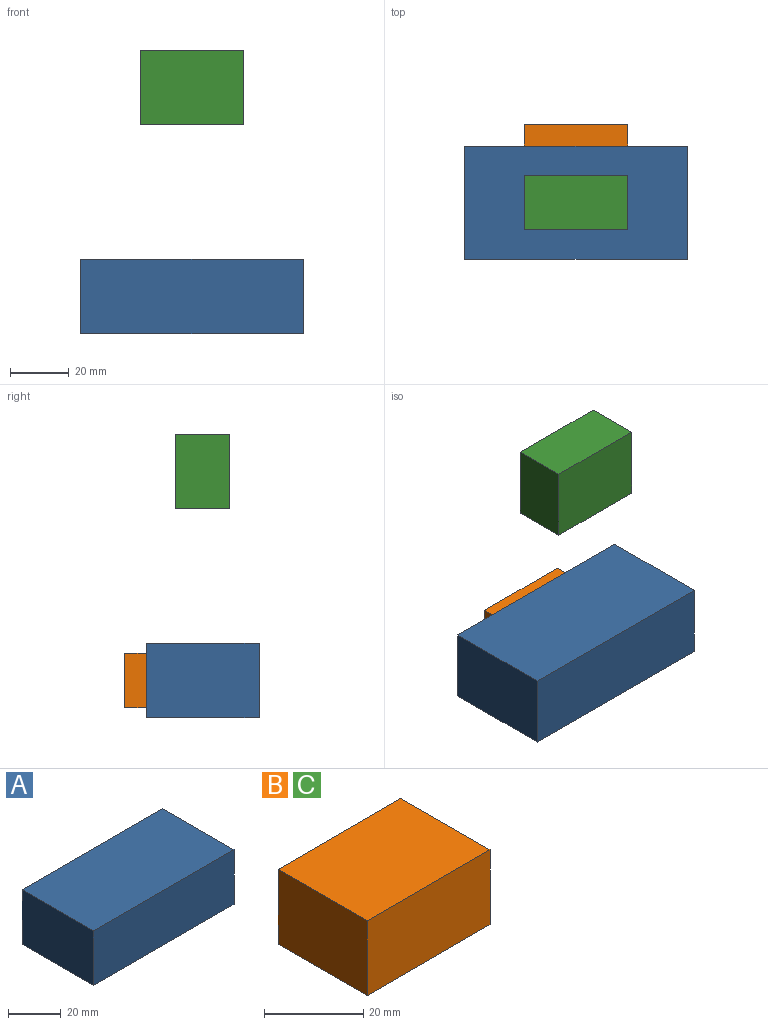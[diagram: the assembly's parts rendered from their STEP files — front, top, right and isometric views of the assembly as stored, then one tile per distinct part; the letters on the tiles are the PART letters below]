
ASSEMBLY  parts=3 mates=2
PART A: 6 faces, bbox 75.6x38.4x25.4 mm
  f0: plane 75.64x25.4mm, normal (0,1,0), area 1921.3mm2, adj f1,f3,f4,f5
  f1: plane 38.41x25.4mm, normal (-1,0,0), area 975.7mm2, adj f0,f2,f4,f5
  f2: plane 75.64x25.4mm, normal (0,-1,0), area 1921.3mm2, adj f1,f3,f4,f5
  f3: plane 38.41x25.4mm, normal (1,0,0), area 975.7mm2, adj f0,f2,f4,f5
  f4: plane 75.64x38.41mm, normal (0,0,1), area 2905.8mm2, adj f0,f1,f2,f3
  f5: plane 75.64x38.41mm, normal (0,0,-1), area 2905.8mm2, adj f0,f1,f2,f3
PART B: 6 faces, bbox 35.1x25.4x18.5 mm
  f0: plane 35.1x25.4mm, normal (0,0,1), area 891.6mm2, adj f1,f3,f4,f5
  f1: plane 25.4x18.49mm, normal (-1,0,0), area 469.6mm2, adj f0,f2,f4,f5
  f2: plane 35.1x25.4mm, normal (0,0,-1), area 891.6mm2, adj f1,f3,f4,f5
  f3: plane 25.4x18.49mm, normal (1,0,0), area 469.6mm2, adj f0,f2,f4,f5
  f4: plane 35.1x18.49mm, normal (0,-1,0), area 649mm2, adj f0,f1,f2,f3
  f5: plane 35.1x18.49mm, normal (0,1,0), area 649mm2, adj f0,f1,f2,f3
PART C: same geometry as B
PLACE A t=(13.41,60.71,20.71)mm fixed
PLACE B rot(axis=(1,0,0),180deg) t=(116.87,35.04,83.87)mm
PLACE C rot(axis=(1,0,0),90deg) t=(116.87,84.42,117.19)mm
MATE slider C.f4 <-> A.f4  axis (0,0,-1) through (39.11,33.96,91.79)mm
MATE slider A.f2 <-> B.f4  axis (0,-1,0) through (39.11,14.76,33.41)mm
